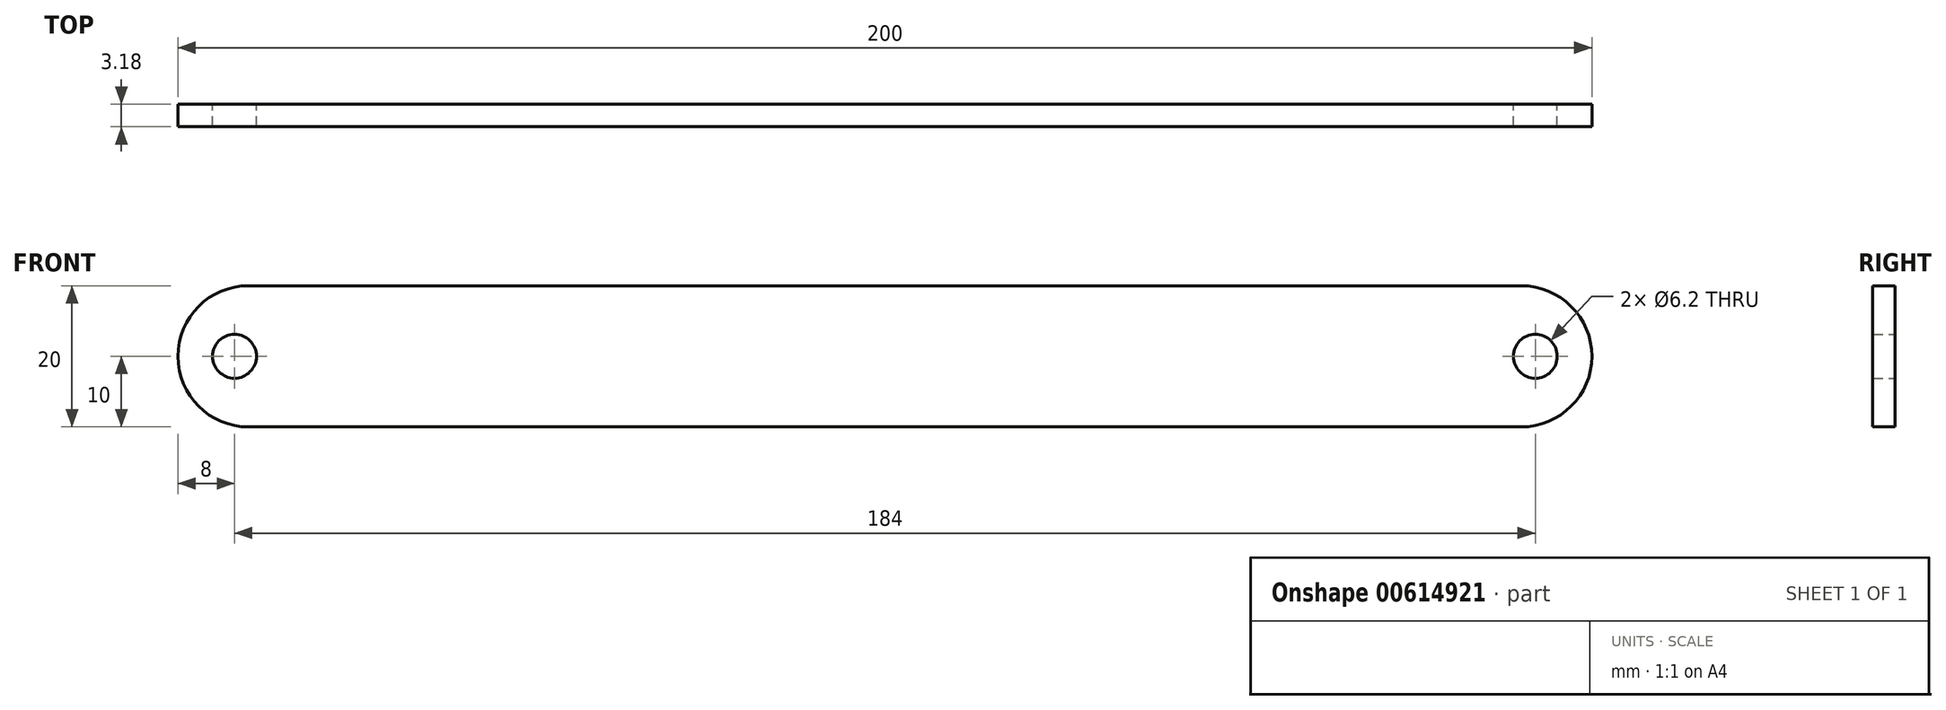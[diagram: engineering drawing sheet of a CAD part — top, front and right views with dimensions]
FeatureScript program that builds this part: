
annotation { "Feature Type Name" : "Feature", "Feature Type Description" : "" }
export const myFeature = defineFeature(function(context is Context, id is Id, definition is map)
    precondition{}
    {
        {
            var Q0;
            Q0=qCreatedBy(makeId("Front.planeOp"),FACE);
            var sketch = newSketch(context, id + "F0", { "sketchPlane" : qUnion([Q0])});
            skLineSegment(sketch, "E0.bottom", {"start": v(90, 10) * mm, "end": v(-90, 10) * mm});
            skLineSegment(sketch, "E0.top", {"start": v(90, -10) * mm, "end": v(-90, -10) * mm});
            skLineSegment(sketch, "E0.left", {"start": v(100, 0) * mm, "end": v(100, 0) * mm});
            skLineSegment(sketch, "E0.right", {"start": v(-100, 0) * mm, "end": v(-100, 0) * mm});
            skPoint(sketch, "E0.middle", {"position": v(0, 0) * mm});
            skLineSegment(sketch, "E1", {"start": v(-100, 0) * mm, "end": v(-92, 0) * mm});
            skCircle(sketch, "E2", {"center": v(-92, 0) * mm, "radius": 3.1 * mm});
            skLineSegment(sketch, "E3", {"start": v(100, 0) * mm, "end": v(92, 0) * mm});
            skCircle(sketch, "E4", {"center": v(92, 0) * mm, "radius": 3.1 * mm});
            skPoint(sketch, "E5.visualSharp", {"position": v(100, 10) * mm});
            skArc(sketch, "E5.filletArc", {"start": v(100, 0) * mm, "mid": v(97.07, 7.07) * mm, "end": v(90, 10) * mm});
            skPoint(sketch, "E6.visualSharp", {"position": v(100, -10) * mm});
            skArc(sketch, "E6.filletArc", {"start": v(90, -10) * mm, "mid": v(97.07, -7.07) * mm, "end": v(100, 0) * mm});
            skPoint(sketch, "E7.visualSharp", {"position": v(-100, -10) * mm});
            skArc(sketch, "E7.filletArc", {"start": v(-100, 0) * mm, "mid": v(-97.07, -7.07) * mm, "end": v(-90, -10) * mm});
            skPoint(sketch, "E8.visualSharp", {"position": v(-100, 10) * mm});
            skArc(sketch, "E8.filletArc", {"start": v(-90, 10) * mm, "mid": v(-97.07, 7.07) * mm, "end": v(-100, 0) * mm});
            skSolve(sketch);
        }
        {
            var Q0;
            Q0 = qSketchRegion(id + "F0", true);
            extrude(context, id + "F1", {"entities" : qUnion([Q0]), "depth" : 3.17 * mm, "offsetDistance" : 25 * mm});
        }
    });
